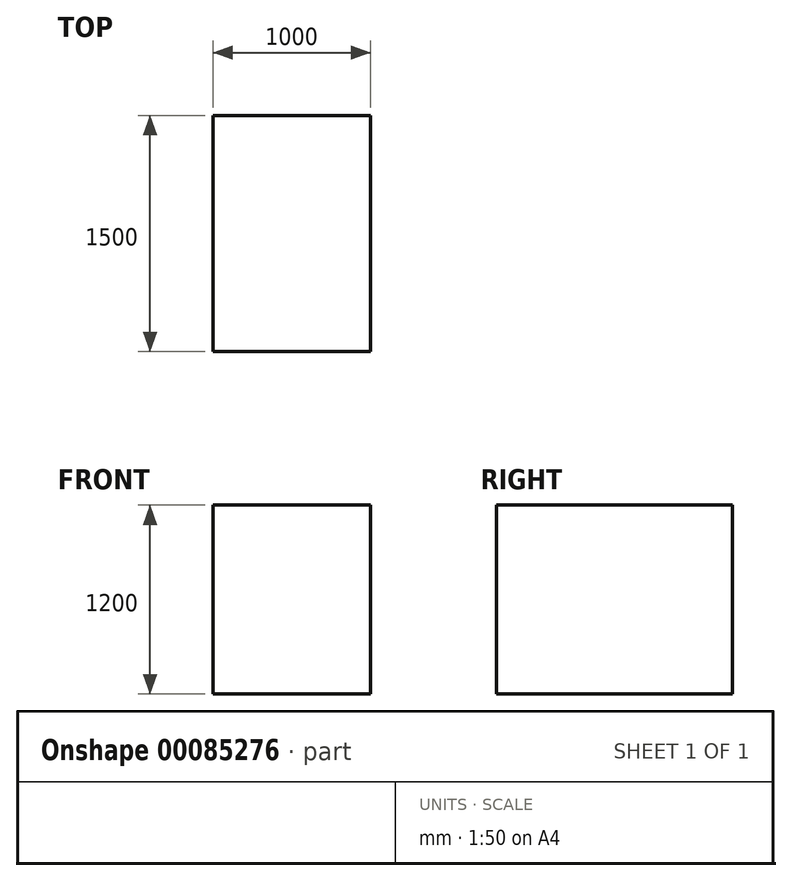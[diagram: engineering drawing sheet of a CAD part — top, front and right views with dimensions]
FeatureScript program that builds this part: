
annotation { "Feature Type Name" : "Feature", "Feature Type Description" : "" }
export const myFeature = defineFeature(function(context is Context, id is Id, definition is map)
    precondition{}
    {
        {
            var Q0;
            Q0=qCreatedBy(makeId("Front.planeOp"),FACE);
            var sketch = newSketch(context, id + "F0", { "sketchPlane" : qUnion([Q0])});
            skLineSegment(sketch, "E0.bottom", {"start": v(0, 0) * mm, "end": v(-1000, 0) * mm});
            skLineSegment(sketch, "E0.top", {"start": v(0, 1200) * mm, "end": v(-1000, 1200) * mm});
            skLineSegment(sketch, "E0.left", {"start": v(0, 0) * mm, "end": v(0, 1200) * mm});
            skLineSegment(sketch, "E0.right", {"start": v(-1000, 0) * mm, "end": v(-1000, 1200) * mm});
            skSolve(sketch);
        }
        {
            var Q0;
            Q0 = qSketchRegion(id + "F0", true);
            extrude(context, id + "F1", {"entities" : qUnion([Q0]), "depth" : 1500 * mm});
        }
    });
